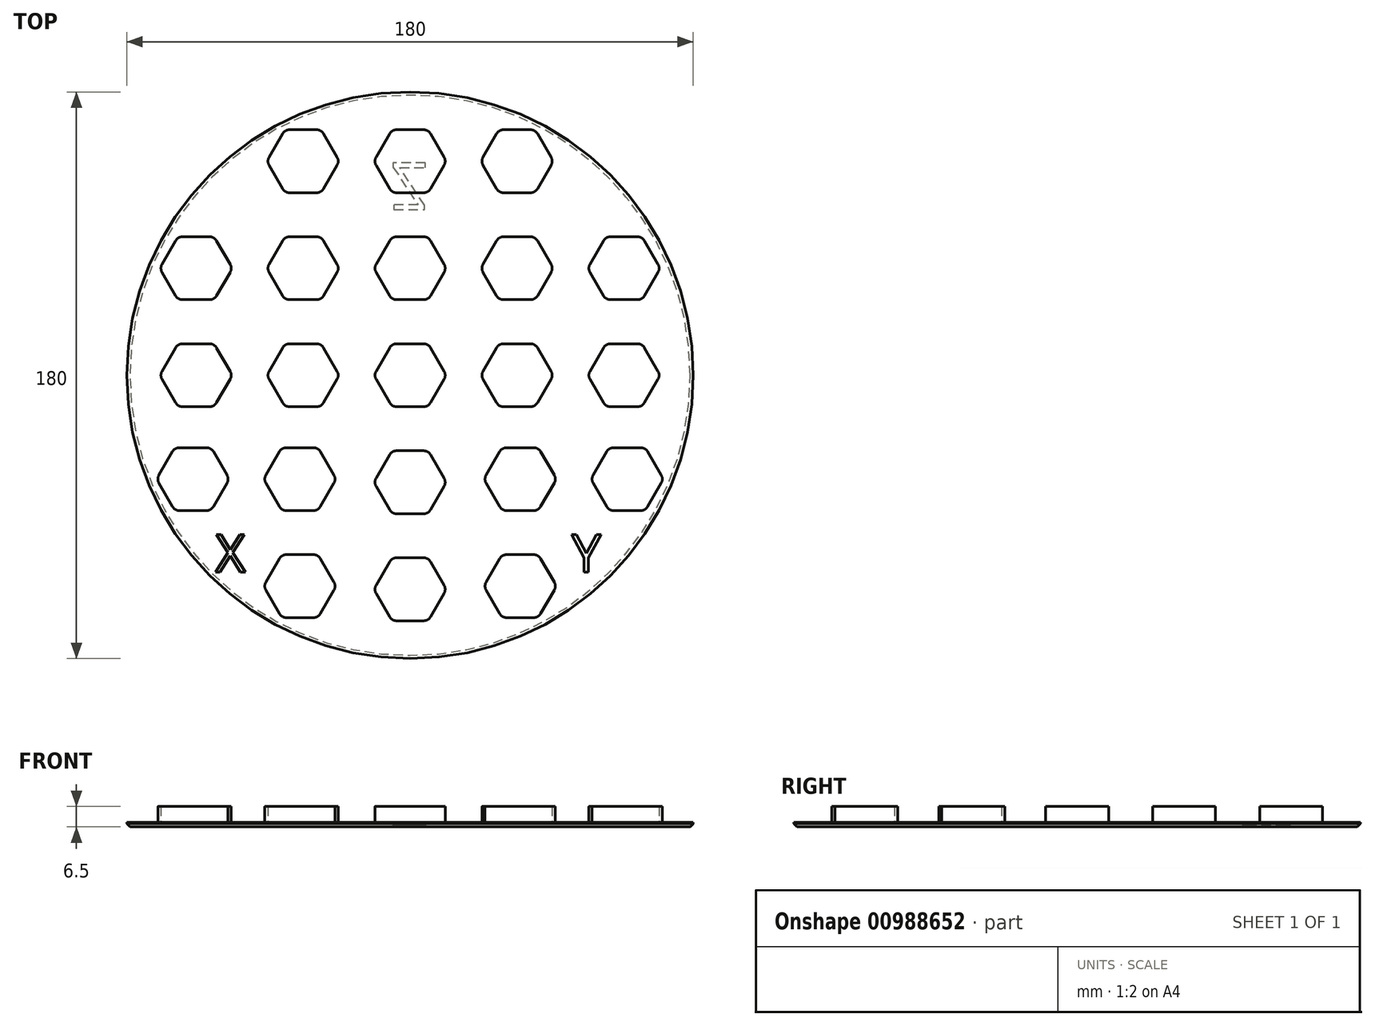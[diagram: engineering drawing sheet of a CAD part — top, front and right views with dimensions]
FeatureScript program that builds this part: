
annotation { "Feature Type Name" : "Feature", "Feature Type Description" : "" }
export const myFeature = defineFeature(function(context is Context, id is Id, definition is map)
    precondition{}
    {
        {
            var Q0;
            Q0=qCreatedBy(makeId("Top.planeOp"),FACE);
            var sketch = newSketch(context, id + "F0", { "sketchPlane" : qUnion([Q0])});
            skCircle(sketch, "E0", {"center": v(0, 0) * mm, "radius": 90 * mm});
            skSolve(sketch);
        }
        {
            var Q0;
            Q0 = qSketchRegion(id + "F0", true);
            extrude(context, id + "F1", {"entities" : qUnion([Q0]), "depth" : 1.5 * mm, "offsetDistance" : 25 * mm});
        }
        {
            var Q0;
            Q0=makeQuery(id+"F1.opExtrude","CAP_FACE",FACE,{"disambiguationData":[OSD([sQuery(id+"F0.wireOp",EDGE,"E0")])],"isStart":false});
            var sketch = newSketch(context, id + "F2", { "sketchPlane" : qUnion([Q0])});
            skCircle(sketch, "E1.cCircle", {"center": v(0, 0) * mm, "radius": 10 * mm, "construction": true});
            skLineSegment(sketch, "E1.0", {"start": v(-5.77, 10) * mm, "end": v(5.77, 10) * mm});
            skLineSegment(sketch, "E1.1", {"start": v(5.77, 10) * mm, "end": v(11.55, 0) * mm});
            skLineSegment(sketch, "E1.2", {"start": v(11.55, 0) * mm, "end": v(5.77, -10) * mm});
            skLineSegment(sketch, "E1.3", {"start": v(5.77, -10) * mm, "end": v(-5.77, -10) * mm});
            skLineSegment(sketch, "E1.4", {"start": v(-5.77, -10) * mm, "end": v(-11.55, 0) * mm});
            skLineSegment(sketch, "E1.5", {"start": v(-11.55, 0) * mm, "end": v(-5.77, 10) * mm});
            skPoint(sketch, "E1.0.midPoint", {"position": v(0, 10) * mm});
            skLineSegment(sketch, "E2", {"start": v(0, 0) * mm, "end": v(90, 0) * mm, "construction": true});
            skLineSegment(sketch, "E3", {"start": v(0, 0) * mm, "end": v(0, 90) * mm, "construction": true});
            skLineSegment(sketch, "E4.0.1.0", {"start": v(11.55, 34) * mm, "end": v(5.77, 24) * mm});
            skLineSegment(sketch, "E4.0.1.1", {"start": v(5.77, 24) * mm, "end": v(-5.77, 24) * mm});
            skPoint(sketch, "E4.0.1.2", {"position": v(0, 44) * mm});
            skCircle(sketch, "E4.0.1.3", {"center": v(0, 34) * mm, "radius": 10 * mm, "construction": true});
            skLineSegment(sketch, "E4.0.1.4", {"start": v(5.77, 44) * mm, "end": v(11.55, 34) * mm});
            skLineSegment(sketch, "E4.0.1.5", {"start": v(-5.77, 44) * mm, "end": v(5.77, 44) * mm});
            skLineSegment(sketch, "E4.0.1.6", {"start": v(-5.77, 24) * mm, "end": v(-11.55, 34) * mm});
            skLineSegment(sketch, "E4.0.1.7", {"start": v(-11.55, 34) * mm, "end": v(-5.77, 44) * mm});
            skLineSegment(sketch, "E4.0.2.0", {"start": v(11.55, 68) * mm, "end": v(5.77, 58) * mm});
            skLineSegment(sketch, "E4.0.2.1", {"start": v(5.77, 58) * mm, "end": v(-5.77, 58) * mm});
            skPoint(sketch, "E4.0.2.2", {"position": v(0, 78) * mm});
            skCircle(sketch, "E4.0.2.3", {"center": v(0, 68) * mm, "radius": 10 * mm, "construction": true});
            skLineSegment(sketch, "E4.0.2.4", {"start": v(5.77, 78) * mm, "end": v(11.55, 68) * mm});
            skLineSegment(sketch, "E4.0.2.5", {"start": v(-5.77, 78) * mm, "end": v(5.77, 78) * mm});
            skLineSegment(sketch, "E4.0.2.6", {"start": v(-5.77, 58) * mm, "end": v(-11.55, 68) * mm});
            skLineSegment(sketch, "E4.0.2.7", {"start": v(-11.55, 68) * mm, "end": v(-5.77, 78) * mm});
            skLineSegment(sketch, "E4.1.0.0", {"start": v(45.55, 0) * mm, "end": v(39.77, -10) * mm});
            skLineSegment(sketch, "E4.1.0.1", {"start": v(39.77, -10) * mm, "end": v(28.23, -10) * mm});
            skPoint(sketch, "E4.1.0.2", {"position": v(34, 10) * mm});
            skCircle(sketch, "E4.1.0.3", {"center": v(34, 0) * mm, "radius": 10 * mm, "construction": true});
            skLineSegment(sketch, "E4.1.0.4", {"start": v(39.77, 10) * mm, "end": v(45.55, 0) * mm});
            skLineSegment(sketch, "E4.1.0.5", {"start": v(28.23, 10) * mm, "end": v(39.77, 10) * mm});
            skLineSegment(sketch, "E4.1.0.6", {"start": v(28.23, -10) * mm, "end": v(22.45, 0) * mm});
            skLineSegment(sketch, "E4.1.0.7", {"start": v(22.45, 0) * mm, "end": v(28.23, 10) * mm});
            skLineSegment(sketch, "E4.1.1.0", {"start": v(45.55, 34) * mm, "end": v(39.77, 24) * mm});
            skLineSegment(sketch, "E4.1.1.1", {"start": v(39.77, 24) * mm, "end": v(28.23, 24) * mm});
            skPoint(sketch, "E4.1.1.2", {"position": v(34, 44) * mm});
            skCircle(sketch, "E4.1.1.3", {"center": v(34, 34) * mm, "radius": 10 * mm, "construction": true});
            skLineSegment(sketch, "E4.1.1.4", {"start": v(39.77, 44) * mm, "end": v(45.55, 34) * mm});
            skLineSegment(sketch, "E4.1.1.5", {"start": v(28.23, 44) * mm, "end": v(39.77, 44) * mm});
            skLineSegment(sketch, "E4.1.1.6", {"start": v(28.23, 24) * mm, "end": v(22.45, 34) * mm});
            skLineSegment(sketch, "E4.1.1.7", {"start": v(22.45, 34) * mm, "end": v(28.23, 44) * mm});
            skLineSegment(sketch, "E4.1.2.0", {"start": v(45.55, 68) * mm, "end": v(39.77, 58) * mm});
            skLineSegment(sketch, "E4.1.2.1", {"start": v(39.77, 58) * mm, "end": v(28.23, 58) * mm});
            skPoint(sketch, "E4.1.2.2", {"position": v(34, 78) * mm});
            skCircle(sketch, "E4.1.2.3", {"center": v(34, 68) * mm, "radius": 10 * mm, "construction": true});
            skLineSegment(sketch, "E4.1.2.4", {"start": v(39.77, 78) * mm, "end": v(45.55, 68) * mm});
            skLineSegment(sketch, "E4.1.2.5", {"start": v(28.23, 78) * mm, "end": v(39.77, 78) * mm});
            skLineSegment(sketch, "E4.1.2.6", {"start": v(28.23, 58) * mm, "end": v(22.45, 68) * mm});
            skLineSegment(sketch, "E4.1.2.7", {"start": v(22.45, 68) * mm, "end": v(28.23, 78) * mm});
            skLineSegment(sketch, "E4.2.0.0", {"start": v(79.55, 0) * mm, "end": v(73.77, -10) * mm});
            skLineSegment(sketch, "E4.2.0.1", {"start": v(73.77, -10) * mm, "end": v(62.23, -10) * mm});
            skPoint(sketch, "E4.2.0.2", {"position": v(68, 10) * mm});
            skCircle(sketch, "E4.2.0.3", {"center": v(68, 0) * mm, "radius": 10 * mm, "construction": true});
            skLineSegment(sketch, "E4.2.0.4", {"start": v(73.77, 10) * mm, "end": v(79.55, 0) * mm});
            skLineSegment(sketch, "E4.2.0.5", {"start": v(62.23, 10) * mm, "end": v(73.77, 10) * mm});
            skLineSegment(sketch, "E4.2.0.6", {"start": v(62.23, -10) * mm, "end": v(56.45, 0) * mm});
            skLineSegment(sketch, "E4.2.0.7", {"start": v(56.45, 0) * mm, "end": v(62.23, 10) * mm});
            skLineSegment(sketch, "E4.2.1.0", {"start": v(79.55, 34) * mm, "end": v(73.77, 24) * mm});
            skLineSegment(sketch, "E4.2.1.1", {"start": v(73.77, 24) * mm, "end": v(62.23, 24) * mm});
            skPoint(sketch, "E4.2.1.2", {"position": v(68, 44) * mm});
            skCircle(sketch, "E4.2.1.3", {"center": v(68, 34) * mm, "radius": 10 * mm, "construction": true});
            skLineSegment(sketch, "E4.2.1.4", {"start": v(73.77, 44) * mm, "end": v(79.55, 34) * mm});
            skLineSegment(sketch, "E4.2.1.5", {"start": v(62.23, 44) * mm, "end": v(73.77, 44) * mm});
            skLineSegment(sketch, "E4.2.1.6", {"start": v(62.23, 24) * mm, "end": v(56.45, 34) * mm});
            skLineSegment(sketch, "E4.2.1.7", {"start": v(56.45, 34) * mm, "end": v(62.23, 44) * mm});
            skLineSegment(sketch, "E4.direction1", {"start": v(-5.77, -10) * mm, "end": v(28.23, -10) * mm, "construction": true});
            skLineSegment(sketch, "E4.direction2", {"start": v(-5.77, -10) * mm, "end": v(-5.77, 24) * mm, "construction": true});
            skCircle(sketch, "E5.1.0", {"center": v(0, -34) * mm, "radius": 10 * mm, "construction": true});
            skLineSegment(sketch, "E5.1.1", {"start": v(11.55, -34) * mm, "end": v(5.77, -44) * mm});
            skLineSegment(sketch, "E5.1.2", {"start": v(-5.77, -58) * mm, "end": v(5.77, -58) * mm});
            skLineSegment(sketch, "E5.1.3", {"start": v(11.55, -68) * mm, "end": v(5.77, -78) * mm});
            skCircle(sketch, "E5.1.4", {"center": v(0, -68) * mm, "radius": 10 * mm, "construction": true});
            skLineSegment(sketch, "E5.1.5", {"start": v(-11.55, -68) * mm, "end": v(-5.77, -58) * mm});
            skPoint(sketch, "E5.1.6", {"position": v(0, -44) * mm});
            skLineSegment(sketch, "E5.1.7", {"start": v(5.77, -24) * mm, "end": v(11.55, -34) * mm});
            skPoint(sketch, "E5.1.8", {"position": v(0, -78) * mm});
            skLineSegment(sketch, "E5.1.9", {"start": v(-11.55, -34) * mm, "end": v(-5.77, -24) * mm});
            skLineSegment(sketch, "E5.1.10", {"start": v(5.77, -44) * mm, "end": v(-5.77, -44) * mm});
            skLineSegment(sketch, "E5.1.11", {"start": v(5.77, -58) * mm, "end": v(11.55, -68) * mm});
            skLineSegment(sketch, "E5.1.12", {"start": v(5.77, -78) * mm, "end": v(-5.77, -78) * mm});
            skLineSegment(sketch, "E5.1.13", {"start": v(-5.77, -24) * mm, "end": v(5.77, -24) * mm});
            skLineSegment(sketch, "E5.1.14", {"start": v(-5.77, -78) * mm, "end": v(-11.55, -68) * mm});
            skLineSegment(sketch, "E5.1.15", {"start": v(-5.77, -44) * mm, "end": v(-11.55, -34) * mm});
            skLineSegment(sketch, "E5.1.16", {"start": v(-39.77, 10) * mm, "end": v(-28.23, 10) * mm});
            skLineSegment(sketch, "E5.1.17", {"start": v(-56.45, 0) * mm, "end": v(-62.23, -10) * mm});
            skLineSegment(sketch, "E5.1.18", {"start": v(-28.23, -10) * mm, "end": v(-39.77, -10) * mm});
            skLineSegment(sketch, "E5.1.19", {"start": v(-22.45, 0) * mm, "end": v(-28.23, -10) * mm});
            skLineSegment(sketch, "E5.1.20", {"start": v(-45.55, 0) * mm, "end": v(-39.77, 10) * mm});
            skLineSegment(sketch, "E5.1.21", {"start": v(-73.77, 10) * mm, "end": v(-62.23, 10) * mm});
            skLineSegment(sketch, "E5.1.22", {"start": v(-62.23, 10) * mm, "end": v(-56.45, 0) * mm});
            skPoint(sketch, "E5.1.23", {"position": v(-68, -10) * mm});
            skCircle(sketch, "E5.1.24", {"center": v(-34, 0) * mm, "radius": 10 * mm, "construction": true});
            skCircle(sketch, "E5.1.25", {"center": v(-68, 0) * mm, "radius": 10 * mm, "construction": true});
            skLineSegment(sketch, "E5.1.26", {"start": v(-79.55, 0) * mm, "end": v(-73.77, 10) * mm});
            skLineSegment(sketch, "E5.1.27", {"start": v(-28.23, 10) * mm, "end": v(-22.45, 0) * mm});
            skPoint(sketch, "E5.1.28", {"position": v(-34, -10) * mm});
            skLineSegment(sketch, "E5.1.29", {"start": v(-62.23, -10) * mm, "end": v(-73.77, -10) * mm});
            skLineSegment(sketch, "E5.1.30", {"start": v(-39.77, -10) * mm, "end": v(-45.55, 0) * mm});
            skLineSegment(sketch, "E5.1.31", {"start": v(-73.77, -10) * mm, "end": v(-79.55, 0) * mm});
            skLineSegment(sketch, "E6.2.0", {"start": v(-29.23, -43) * mm, "end": v(-40.77, -43) * mm});
            skPoint(sketch, "E6.2.1", {"position": v(-35, -77) * mm});
            skLineSegment(sketch, "E6.2.2", {"start": v(-63.23, -23) * mm, "end": v(-57.45, -33) * mm});
            skLineSegment(sketch, "E6.2.3", {"start": v(-29.23, -57) * mm, "end": v(-23.45, -67) * mm});
            skPoint(sketch, "E6.2.4", {"position": v(-69, -43) * mm});
            skLineSegment(sketch, "E6.2.5", {"start": v(-40.77, -77) * mm, "end": v(-46.55, -67) * mm});
            skCircle(sketch, "E6.2.6", {"center": v(-35, -33) * mm, "radius": 10 * mm, "construction": true});
            skLineSegment(sketch, "E6.2.7", {"start": v(-74.77, -43) * mm, "end": v(-80.55, -33) * mm});
            skLineSegment(sketch, "E6.2.8", {"start": v(-40.77, -43) * mm, "end": v(-46.55, -33) * mm});
            skLineSegment(sketch, "E6.2.9", {"start": v(-80.55, -33) * mm, "end": v(-74.77, -23) * mm});
            skLineSegment(sketch, "E6.2.10", {"start": v(-40.77, -23) * mm, "end": v(-29.23, -23) * mm});
            skPoint(sketch, "E6.2.11", {"position": v(-35, -43) * mm});
            skLineSegment(sketch, "E6.2.12", {"start": v(-46.55, -67) * mm, "end": v(-40.77, -57) * mm});
            skLineSegment(sketch, "E6.2.13", {"start": v(-46.55, -33) * mm, "end": v(-40.77, -23) * mm});
            skLineSegment(sketch, "E6.2.14", {"start": v(-29.23, -23) * mm, "end": v(-23.45, -33) * mm});
            skLineSegment(sketch, "E6.2.15", {"start": v(-23.45, -67) * mm, "end": v(-29.23, -77) * mm});
            skLineSegment(sketch, "E6.2.16", {"start": v(-63.23, -43) * mm, "end": v(-74.77, -43) * mm});
            skLineSegment(sketch, "E6.2.17", {"start": v(-23.45, -33) * mm, "end": v(-29.23, -43) * mm});
            skLineSegment(sketch, "E6.2.18", {"start": v(-29.23, -77) * mm, "end": v(-40.77, -77) * mm});
            skCircle(sketch, "E6.2.19", {"center": v(-69, -33) * mm, "radius": 10 * mm, "construction": true});
            skLineSegment(sketch, "E6.2.20", {"start": v(-57.45, -33) * mm, "end": v(-63.23, -43) * mm});
            skLineSegment(sketch, "E6.2.21", {"start": v(-40.77, -57) * mm, "end": v(-29.23, -57) * mm});
            skCircle(sketch, "E6.2.22", {"center": v(-35, -67) * mm, "radius": 10 * mm, "construction": true});
            skLineSegment(sketch, "E6.2.23", {"start": v(-74.77, -23) * mm, "end": v(-63.23, -23) * mm});
            skPoint(sketch, "E6.center", {"position": v(-0.5, 0.5) * mm});
            skLineSegment(sketch, "E7.MirrorCS", {"start": v(-28.23, 24) * mm, "end": v(-22.45, 34) * mm});
            skLineSegment(sketch, "E8.MirrorCS", {"start": v(-28.23, 78) * mm, "end": v(-39.77, 78) * mm});
            skLineSegment(sketch, "E9.MirrorCS", {"start": v(-28.23, 44) * mm, "end": v(-39.77, 44) * mm});
            skLineSegment(sketch, "E10.MirrorCS", {"start": v(-62.23, 44) * mm, "end": v(-73.77, 44) * mm});
            skLineSegment(sketch, "E11.MirrorCS", {"start": v(-39.77, 44) * mm, "end": v(-45.55, 34) * mm});
            skLineSegment(sketch, "E12.MirrorCS", {"start": v(-73.77, 24) * mm, "end": v(-62.23, 24) * mm});
            skLineSegment(sketch, "E13.MirrorCS", {"start": v(-62.23, 24) * mm, "end": v(-56.45, 34) * mm});
            skLineSegment(sketch, "E14.MirrorCS", {"start": v(-39.77, 24) * mm, "end": v(-28.23, 24) * mm});
            skLineSegment(sketch, "E15.MirrorCS", {"start": v(-73.77, 44) * mm, "end": v(-79.55, 34) * mm});
            skLineSegment(sketch, "E16.MirrorCS", {"start": v(-45.55, 68) * mm, "end": v(-39.77, 58) * mm});
            skPoint(sketch, "E17.MirrorP", {"position": v(-34, 44) * mm});
            skLineSegment(sketch, "E18.MirrorCS", {"start": v(-22.45, 68) * mm, "end": v(-28.23, 78) * mm});
            skCircle(sketch, "E19.MirrorC", {"center": v(-34, 68) * mm, "radius": 10 * mm, "construction": true});
            skLineSegment(sketch, "E20.MirrorCS", {"start": v(-79.55, 34) * mm, "end": v(-73.77, 24) * mm});
            skPoint(sketch, "E21.MirrorP", {"position": v(-34, 78) * mm});
            skLineSegment(sketch, "E22.MirrorCS", {"start": v(-28.23, 58) * mm, "end": v(-22.45, 68) * mm});
            skPoint(sketch, "E23.MirrorP", {"position": v(-68, 44) * mm});
            skLineSegment(sketch, "E24.MirrorCS", {"start": v(-39.77, 58) * mm, "end": v(-28.23, 58) * mm});
            skCircle(sketch, "E25.MirrorC", {"center": v(-68, 34) * mm, "radius": 10 * mm, "construction": true});
            skLineSegment(sketch, "E26.MirrorCS", {"start": v(-45.55, 34) * mm, "end": v(-39.77, 24) * mm});
            skLineSegment(sketch, "E27.MirrorCS", {"start": v(-22.45, 34) * mm, "end": v(-28.23, 44) * mm});
            skLineSegment(sketch, "E28.MirrorCS", {"start": v(-39.77, 78) * mm, "end": v(-45.55, 68) * mm});
            skCircle(sketch, "E29.MirrorC", {"center": v(-34, 34) * mm, "radius": 10 * mm, "construction": true});
            skLineSegment(sketch, "E30.MirrorCS", {"start": v(-56.45, 34) * mm, "end": v(-62.23, 44) * mm});
            skLineSegment(sketch, "E31.MirrorCS", {"start": v(63.23, -43) * mm, "end": v(74.77, -43) * mm});
            skLineSegment(sketch, "E32.MirrorCS", {"start": v(74.77, -43) * mm, "end": v(80.55, -33) * mm});
            skLineSegment(sketch, "E33.MirrorCS", {"start": v(80.55, -33) * mm, "end": v(74.77, -23) * mm});
            skLineSegment(sketch, "E34.MirrorCS", {"start": v(29.23, -77) * mm, "end": v(40.77, -77) * mm});
            skLineSegment(sketch, "E35.MirrorCS", {"start": v(74.77, -23) * mm, "end": v(63.23, -23) * mm});
            skLineSegment(sketch, "E36.MirrorCS", {"start": v(29.23, -43) * mm, "end": v(40.77, -43) * mm});
            skLineSegment(sketch, "E37.MirrorCS", {"start": v(57.45, -33) * mm, "end": v(63.23, -43) * mm});
            skPoint(sketch, "E38.MirrorP", {"position": v(69, -43) * mm});
            skLineSegment(sketch, "E39.MirrorCS", {"start": v(29.23, -57) * mm, "end": v(23.45, -67) * mm});
            skLineSegment(sketch, "E40.MirrorCS", {"start": v(40.77, -23) * mm, "end": v(29.23, -23) * mm});
            skLineSegment(sketch, "E41.MirrorCS", {"start": v(40.77, -57) * mm, "end": v(29.23, -57) * mm});
            skCircle(sketch, "E42.MirrorC", {"center": v(35, -33) * mm, "radius": 10 * mm, "construction": true});
            skLineSegment(sketch, "E43.MirrorCS", {"start": v(23.45, -67) * mm, "end": v(29.23, -77) * mm});
            skLineSegment(sketch, "E44.MirrorCS", {"start": v(63.23, -23) * mm, "end": v(57.45, -33) * mm});
            skLineSegment(sketch, "E45.MirrorCS", {"start": v(46.55, -67) * mm, "end": v(40.77, -57) * mm});
            skCircle(sketch, "E46.MirrorC", {"center": v(69, -33) * mm, "radius": 10 * mm, "construction": true});
            skPoint(sketch, "E47.MirrorP", {"position": v(35, -43) * mm});
            skLineSegment(sketch, "E48.MirrorCS", {"start": v(29.23, -23) * mm, "end": v(23.45, -33) * mm});
            skPoint(sketch, "E49.MirrorP", {"position": v(35, -77) * mm});
            skLineSegment(sketch, "E50.MirrorCS", {"start": v(40.77, -43) * mm, "end": v(46.55, -33) * mm});
            skLineSegment(sketch, "E51.MirrorCS", {"start": v(40.77, -77) * mm, "end": v(46.55, -67) * mm});
            skLineSegment(sketch, "E52.MirrorCS", {"start": v(46.55, -33) * mm, "end": v(40.77, -23) * mm});
            skLineSegment(sketch, "E53.MirrorCS", {"start": v(23.45, -33) * mm, "end": v(29.23, -43) * mm});
            skCircle(sketch, "E54.MirrorC", {"center": v(35, -67) * mm, "radius": 10 * mm, "construction": true});
            skSolve(sketch);
        }
        {
            var Q0;
            Q0 = qSketchRegion(id + "F2", true);
            extrude(context, id + "F3", {"entities" : qUnion([Q0]), "operationType" : NewBodyOperationType.ADD, "depth" : 5 * mm, "offsetDistance" : 25 * mm});
        }
        {
            var Q0;
            Q0=makeQuery(id+"F3.opExtrude","SWEPT_EDGE",EDGE,{"disambiguationData":[OSD([sQuery(id+"F2.wireOp",EDGE,"E6.2.5"),sQuery(id+"F2.wireOp",EDGE,"E6.2.18")])]});
            var Q1;
            Q1=makeQuery(id+"F3.opExtrude","SWEPT_EDGE",EDGE,{"disambiguationData":[OSD([sQuery(id+"F2.wireOp",EDGE,"E6.2.15"),sQuery(id+"F2.wireOp",EDGE,"E6.2.18")])]});
            var Q2;
            Q2=makeQuery(id+"F3.opExtrude","SWEPT_EDGE",EDGE,{"disambiguationData":[OSD([sQuery(id+"F2.wireOp",EDGE,"E6.2.3"),sQuery(id+"F2.wireOp",EDGE,"E6.2.15")])]});
            var Q3;
            Q3=makeQuery(id+"F3.opExtrude","SWEPT_EDGE",EDGE,{"disambiguationData":[OSD([sQuery(id+"F2.wireOp",EDGE,"E6.2.5"),sQuery(id+"F2.wireOp",EDGE,"E6.2.12")])]});
            var Q4;
            Q4=makeQuery(id+"F3.opExtrude","SWEPT_EDGE",EDGE,{"disambiguationData":[OSD([sQuery(id+"F2.wireOp",EDGE,"E6.2.12"),sQuery(id+"F2.wireOp",EDGE,"E6.2.21")])]});
            var Q5;
            Q5=makeQuery(id+"F3.opExtrude","SWEPT_EDGE",EDGE,{"disambiguationData":[OSD([sQuery(id+"F2.wireOp",EDGE,"E6.2.3"),sQuery(id+"F2.wireOp",EDGE,"E6.2.21")])]});
            var Q6;
            Q6=makeQuery(id+"F3.opExtrude","SWEPT_EDGE",EDGE,{"disambiguationData":[OSD([sQuery(id+"F2.wireOp",EDGE,"E5.1.12"),sQuery(id+"F2.wireOp",EDGE,"E5.1.14")])]});
            var Q7;
            Q7=makeQuery(id+"F3.opExtrude","SWEPT_EDGE",EDGE,{"disambiguationData":[OSD([sQuery(id+"F2.wireOp",EDGE,"E5.1.3"),sQuery(id+"F2.wireOp",EDGE,"E5.1.12")])]});
            var Q8;
            Q8=makeQuery(id+"F3.opExtrude","SWEPT_EDGE",EDGE,{"disambiguationData":[OSD([sQuery(id+"F2.wireOp",EDGE,"E5.1.3"),sQuery(id+"F2.wireOp",EDGE,"E5.1.11")])]});
            var Q9;
            Q9=makeQuery(id+"F3.opExtrude","SWEPT_EDGE",EDGE,{"disambiguationData":[OSD([sQuery(id+"F2.wireOp",EDGE,"E5.1.5"),sQuery(id+"F2.wireOp",EDGE,"E5.1.14")])]});
            var Q10;
            Q10=makeQuery(id+"F3.opExtrude","SWEPT_EDGE",EDGE,{"disambiguationData":[OSD([sQuery(id+"F2.wireOp",EDGE,"E5.1.2"),sQuery(id+"F2.wireOp",EDGE,"E5.1.5")])]});
            var Q11;
            Q11=makeQuery(id+"F3.opExtrude","SWEPT_EDGE",EDGE,{"disambiguationData":[OSD([sQuery(id+"F2.wireOp",EDGE,"E5.1.2"),sQuery(id+"F2.wireOp",EDGE,"E5.1.11")])]});
            var Q12;
            Q12=makeQuery(id+"F3.opExtrude","SWEPT_EDGE",EDGE,{"disambiguationData":[OSD([sQuery(id+"F2.wireOp",EDGE,"E39.MirrorCS"),sQuery(id+"F2.wireOp",EDGE,"E43.MirrorCS")])]});
            var Q13;
            Q13=makeQuery(id+"F3.opExtrude","SWEPT_EDGE",EDGE,{"disambiguationData":[OSD([sQuery(id+"F2.wireOp",EDGE,"E39.MirrorCS"),sQuery(id+"F2.wireOp",EDGE,"E41.MirrorCS")])]});
            var Q14;
            Q14=makeQuery(id+"F3.opExtrude","SWEPT_EDGE",EDGE,{"disambiguationData":[OSD([sQuery(id+"F2.wireOp",EDGE,"E41.MirrorCS"),sQuery(id+"F2.wireOp",EDGE,"E45.MirrorCS")])]});
            var Q15;
            Q15=makeQuery(id+"F3.opExtrude","SWEPT_EDGE",EDGE,{"disambiguationData":[OSD([sQuery(id+"F2.wireOp",EDGE,"E34.MirrorCS"),sQuery(id+"F2.wireOp",EDGE,"E43.MirrorCS")])]});
            var Q16;
            Q16=makeQuery(id+"F3.opExtrude","SWEPT_EDGE",EDGE,{"disambiguationData":[OSD([sQuery(id+"F2.wireOp",EDGE,"E45.MirrorCS"),sQuery(id+"F2.wireOp",EDGE,"E51.MirrorCS")])]});
            var Q17;
            Q17=makeQuery(id+"F3.opExtrude","SWEPT_EDGE",EDGE,{"disambiguationData":[OSD([sQuery(id+"F2.wireOp",EDGE,"E34.MirrorCS"),sQuery(id+"F2.wireOp",EDGE,"E51.MirrorCS")])]});
            var Q18;
            Q18=makeQuery(id+"F3.opExtrude","SWEPT_EDGE",EDGE,{"disambiguationData":[OSD([sQuery(id+"F2.wireOp",EDGE,"E6.2.7"),sQuery(id+"F2.wireOp",EDGE,"E6.2.16")])]});
            var Q19;
            Q19=makeQuery(id+"F3.opExtrude","SWEPT_EDGE",EDGE,{"disambiguationData":[OSD([sQuery(id+"F2.wireOp",EDGE,"E6.2.16"),sQuery(id+"F2.wireOp",EDGE,"E6.2.20")])]});
            var Q20;
            Q20=makeQuery(id+"F3.opExtrude","SWEPT_EDGE",EDGE,{"disambiguationData":[OSD([sQuery(id+"F2.wireOp",EDGE,"E6.2.2"),sQuery(id+"F2.wireOp",EDGE,"E6.2.20")])]});
            var Q21;
            Q21=makeQuery(id+"F3.opExtrude","SWEPT_EDGE",EDGE,{"disambiguationData":[OSD([sQuery(id+"F2.wireOp",EDGE,"E6.2.2"),sQuery(id+"F2.wireOp",EDGE,"E6.2.23")])]});
            var Q22;
            Q22=makeQuery(id+"F3.opExtrude","SWEPT_EDGE",EDGE,{"disambiguationData":[OSD([sQuery(id+"F2.wireOp",EDGE,"E6.2.9"),sQuery(id+"F2.wireOp",EDGE,"E6.2.23")])]});
            var Q23;
            Q23=makeQuery(id+"F3.opExtrude","SWEPT_EDGE",EDGE,{"disambiguationData":[OSD([sQuery(id+"F2.wireOp",EDGE,"E6.2.7"),sQuery(id+"F2.wireOp",EDGE,"E6.2.9")])]});
            var Q24;
            Q24=makeQuery(id+"F3.opExtrude","SWEPT_EDGE",EDGE,{"disambiguationData":[OSD([sQuery(id+"F2.wireOp",EDGE,"E6.2.10"),sQuery(id+"F2.wireOp",EDGE,"E6.2.13")])]});
            var Q25;
            Q25=makeQuery(id+"F3.opExtrude","SWEPT_EDGE",EDGE,{"disambiguationData":[OSD([sQuery(id+"F2.wireOp",EDGE,"E6.2.8"),sQuery(id+"F2.wireOp",EDGE,"E6.2.13")])]});
            var Q26;
            Q26=makeQuery(id+"F3.opExtrude","SWEPT_EDGE",EDGE,{"disambiguationData":[OSD([sQuery(id+"F2.wireOp",EDGE,"E6.2.0"),sQuery(id+"F2.wireOp",EDGE,"E6.2.8")])]});
            var Q27;
            Q27=makeQuery(id+"F3.opExtrude","SWEPT_EDGE",EDGE,{"disambiguationData":[OSD([sQuery(id+"F2.wireOp",EDGE,"E6.2.0"),sQuery(id+"F2.wireOp",EDGE,"E6.2.17")])]});
            var Q28;
            Q28=makeQuery(id+"F3.opExtrude","SWEPT_EDGE",EDGE,{"disambiguationData":[OSD([sQuery(id+"F2.wireOp",EDGE,"E6.2.14"),sQuery(id+"F2.wireOp",EDGE,"E6.2.17")])]});
            var Q29;
            Q29=makeQuery(id+"F3.opExtrude","SWEPT_EDGE",EDGE,{"disambiguationData":[OSD([sQuery(id+"F2.wireOp",EDGE,"E6.2.10"),sQuery(id+"F2.wireOp",EDGE,"E6.2.14")])]});
            var Q30;
            Q30=makeQuery(id+"F3.opExtrude","SWEPT_EDGE",EDGE,{"disambiguationData":[OSD([sQuery(id+"F2.wireOp",EDGE,"E5.1.9"),sQuery(id+"F2.wireOp",EDGE,"E5.1.15")])]});
            var Q31;
            Q31=makeQuery(id+"F3.opExtrude","SWEPT_EDGE",EDGE,{"disambiguationData":[OSD([sQuery(id+"F2.wireOp",EDGE,"E5.1.9"),sQuery(id+"F2.wireOp",EDGE,"E5.1.13")])]});
            var Q32;
            Q32=makeQuery(id+"F3.opExtrude","SWEPT_EDGE",EDGE,{"disambiguationData":[OSD([sQuery(id+"F2.wireOp",EDGE,"E5.1.10"),sQuery(id+"F2.wireOp",EDGE,"E5.1.15")])]});
            var Q33;
            Q33=makeQuery(id+"F3.opExtrude","SWEPT_EDGE",EDGE,{"disambiguationData":[OSD([sQuery(id+"F2.wireOp",EDGE,"E5.1.1"),sQuery(id+"F2.wireOp",EDGE,"E5.1.10")])]});
            var Q34;
            Q34=makeQuery(id+"F3.opExtrude","SWEPT_EDGE",EDGE,{"disambiguationData":[OSD([sQuery(id+"F2.wireOp",EDGE,"E5.1.1"),sQuery(id+"F2.wireOp",EDGE,"E5.1.7")])]});
            var Q35;
            Q35=makeQuery(id+"F3.opExtrude","SWEPT_EDGE",EDGE,{"disambiguationData":[OSD([sQuery(id+"F2.wireOp",EDGE,"E5.1.7"),sQuery(id+"F2.wireOp",EDGE,"E5.1.13")])]});
            var Q36;
            Q36=makeQuery(id+"F3.opExtrude","SWEPT_EDGE",EDGE,{"disambiguationData":[OSD([sQuery(id+"F2.wireOp",EDGE,"E48.MirrorCS"),sQuery(id+"F2.wireOp",EDGE,"E53.MirrorCS")])]});
            var Q37;
            Q37=makeQuery(id+"F3.opExtrude","SWEPT_EDGE",EDGE,{"disambiguationData":[OSD([sQuery(id+"F2.wireOp",EDGE,"E36.MirrorCS"),sQuery(id+"F2.wireOp",EDGE,"E53.MirrorCS")])]});
            var Q38;
            Q38=makeQuery(id+"F3.opExtrude","SWEPT_EDGE",EDGE,{"disambiguationData":[OSD([sQuery(id+"F2.wireOp",EDGE,"E50.MirrorCS"),sQuery(id+"F2.wireOp",EDGE,"E52.MirrorCS")])]});
            var Q39;
            Q39=makeQuery(id+"F3.opExtrude","SWEPT_EDGE",EDGE,{"disambiguationData":[OSD([sQuery(id+"F2.wireOp",EDGE,"E40.MirrorCS"),sQuery(id+"F2.wireOp",EDGE,"E52.MirrorCS")])]});
            var Q40;
            Q40=makeQuery(id+"F3.opExtrude","SWEPT_EDGE",EDGE,{"disambiguationData":[OSD([sQuery(id+"F2.wireOp",EDGE,"E40.MirrorCS"),sQuery(id+"F2.wireOp",EDGE,"E48.MirrorCS")])]});
            var Q41;
            Q41=makeQuery(id+"F3.opExtrude","SWEPT_EDGE",EDGE,{"disambiguationData":[OSD([sQuery(id+"F2.wireOp",EDGE,"E36.MirrorCS"),sQuery(id+"F2.wireOp",EDGE,"E50.MirrorCS")])]});
            var Q42;
            Q42=makeQuery(id+"F3.opExtrude","SWEPT_EDGE",EDGE,{"disambiguationData":[OSD([sQuery(id+"F2.wireOp",EDGE,"E31.MirrorCS"),sQuery(id+"F2.wireOp",EDGE,"E37.MirrorCS")])]});
            var Q43;
            Q43=makeQuery(id+"F3.opExtrude","SWEPT_EDGE",EDGE,{"disambiguationData":[OSD([sQuery(id+"F2.wireOp",EDGE,"E31.MirrorCS"),sQuery(id+"F2.wireOp",EDGE,"E32.MirrorCS")])]});
            var Q44;
            Q44=makeQuery(id+"F3.opExtrude","SWEPT_EDGE",EDGE,{"disambiguationData":[OSD([sQuery(id+"F2.wireOp",EDGE,"E32.MirrorCS"),sQuery(id+"F2.wireOp",EDGE,"E33.MirrorCS")])]});
            var Q45;
            Q45=makeQuery(id+"F3.opExtrude","SWEPT_EDGE",EDGE,{"disambiguationData":[OSD([sQuery(id+"F2.wireOp",EDGE,"E33.MirrorCS"),sQuery(id+"F2.wireOp",EDGE,"E35.MirrorCS")])]});
            var Q46;
            Q46=makeQuery(id+"F3.opExtrude","SWEPT_EDGE",EDGE,{"disambiguationData":[OSD([sQuery(id+"F2.wireOp",EDGE,"E35.MirrorCS"),sQuery(id+"F2.wireOp",EDGE,"E44.MirrorCS")])]});
            var Q47;
            Q47=makeQuery(id+"F3.opExtrude","SWEPT_EDGE",EDGE,{"disambiguationData":[OSD([sQuery(id+"F2.wireOp",EDGE,"E37.MirrorCS"),sQuery(id+"F2.wireOp",EDGE,"E44.MirrorCS")])]});
            var Q48;
            Q48=makeQuery(id+"F3.opExtrude","SWEPT_EDGE",EDGE,{"disambiguationData":[OSD([sQuery(id+"F2.wireOp",EDGE,"E4.2.0.0"),sQuery(id+"F2.wireOp",EDGE,"E4.2.0.1")])]});
            var Q49;
            Q49=makeQuery(id+"F3.opExtrude","SWEPT_EDGE",EDGE,{"disambiguationData":[OSD([sQuery(id+"F2.wireOp",EDGE,"E4.2.0.1"),sQuery(id+"F2.wireOp",EDGE,"E4.2.0.6")])]});
            var Q50;
            Q50=makeQuery(id+"F3.opExtrude","SWEPT_EDGE",EDGE,{"disambiguationData":[OSD([sQuery(id+"F2.wireOp",EDGE,"E4.2.0.0"),sQuery(id+"F2.wireOp",EDGE,"E4.2.0.4")])]});
            var Q51;
            Q51=makeQuery(id+"F3.opExtrude","SWEPT_EDGE",EDGE,{"disambiguationData":[OSD([sQuery(id+"F2.wireOp",EDGE,"E4.2.0.6"),sQuery(id+"F2.wireOp",EDGE,"E4.2.0.7")])]});
            var Q52;
            Q52=makeQuery(id+"F3.opExtrude","SWEPT_EDGE",EDGE,{"disambiguationData":[OSD([sQuery(id+"F2.wireOp",EDGE,"E4.2.0.5"),sQuery(id+"F2.wireOp",EDGE,"E4.2.0.7")])]});
            var Q53;
            Q53=makeQuery(id+"F3.opExtrude","SWEPT_EDGE",EDGE,{"disambiguationData":[OSD([sQuery(id+"F2.wireOp",EDGE,"E4.2.0.4"),sQuery(id+"F2.wireOp",EDGE,"E4.2.0.5")])]});
            var Q54;
            Q54=makeQuery(id+"F3.opExtrude","SWEPT_EDGE",EDGE,{"disambiguationData":[OSD([sQuery(id+"F2.wireOp",EDGE,"E4.1.0.4"),sQuery(id+"F2.wireOp",EDGE,"E4.1.0.5")])]});
            var Q55;
            Q55=makeQuery(id+"F3.opExtrude","SWEPT_EDGE",EDGE,{"disambiguationData":[OSD([sQuery(id+"F2.wireOp",EDGE,"E4.1.0.5"),sQuery(id+"F2.wireOp",EDGE,"E4.1.0.7")])]});
            var Q56;
            Q56=makeQuery(id+"F3.opExtrude","SWEPT_EDGE",EDGE,{"disambiguationData":[OSD([sQuery(id+"F2.wireOp",EDGE,"E4.1.0.6"),sQuery(id+"F2.wireOp",EDGE,"E4.1.0.7")])]});
            var Q57;
            Q57=makeQuery(id+"F3.opExtrude","SWEPT_EDGE",EDGE,{"disambiguationData":[OSD([sQuery(id+"F2.wireOp",EDGE,"E4.1.0.1"),sQuery(id+"F2.wireOp",EDGE,"E4.1.0.6")])]});
            var Q58;
            Q58=makeQuery(id+"F3.opExtrude","SWEPT_EDGE",EDGE,{"disambiguationData":[OSD([sQuery(id+"F2.wireOp",EDGE,"E4.1.0.0"),sQuery(id+"F2.wireOp",EDGE,"E4.1.0.1")])]});
            var Q59;
            Q59=makeQuery(id+"F3.opExtrude","SWEPT_EDGE",EDGE,{"disambiguationData":[OSD([sQuery(id+"F2.wireOp",EDGE,"E4.1.0.0"),sQuery(id+"F2.wireOp",EDGE,"E4.1.0.4")])]});
            var Q60;
            Q60=makeQuery(id+"F3.opExtrude","SWEPT_EDGE",EDGE,{"disambiguationData":[OSD([sQuery(id+"F2.wireOp",EDGE,"E1.2"),sQuery(id+"F2.wireOp",EDGE,"E1.3")])]});
            var Q61;
            Q61=makeQuery(id+"F3.opExtrude","SWEPT_EDGE",EDGE,{"disambiguationData":[OSD([sQuery(id+"F2.wireOp",EDGE,"E1.1"),sQuery(id+"F2.wireOp",EDGE,"E1.2")])]});
            var Q62;
            Q62=makeQuery(id+"F3.opExtrude","SWEPT_EDGE",EDGE,{"disambiguationData":[OSD([sQuery(id+"F2.wireOp",EDGE,"E1.3"),sQuery(id+"F2.wireOp",EDGE,"E1.4")])]});
            var Q63;
            Q63=makeQuery(id+"F3.opExtrude","SWEPT_EDGE",EDGE,{"disambiguationData":[OSD([sQuery(id+"F2.wireOp",EDGE,"E1.4"),sQuery(id+"F2.wireOp",EDGE,"E1.5")])]});
            var Q64;
            Q64=makeQuery(id+"F3.opExtrude","SWEPT_EDGE",EDGE,{"disambiguationData":[OSD([sQuery(id+"F2.wireOp",EDGE,"E1.0"),sQuery(id+"F2.wireOp",EDGE,"E1.5")])]});
            var Q65;
            Q65=makeQuery(id+"F3.opExtrude","SWEPT_EDGE",EDGE,{"disambiguationData":[OSD([sQuery(id+"F2.wireOp",EDGE,"E1.0"),sQuery(id+"F2.wireOp",EDGE,"E1.1")])]});
            var Q66;
            Q66=makeQuery(id+"F3.opExtrude","SWEPT_EDGE",EDGE,{"disambiguationData":[OSD([sQuery(id+"F2.wireOp",EDGE,"E5.1.16"),sQuery(id+"F2.wireOp",EDGE,"E5.1.20")])]});
            var Q67;
            Q67=makeQuery(id+"F3.opExtrude","SWEPT_EDGE",EDGE,{"disambiguationData":[OSD([sQuery(id+"F2.wireOp",EDGE,"E5.1.20"),sQuery(id+"F2.wireOp",EDGE,"E5.1.30")])]});
            var Q68;
            Q68=makeQuery(id+"F3.opExtrude","SWEPT_EDGE",EDGE,{"disambiguationData":[OSD([sQuery(id+"F2.wireOp",EDGE,"E5.1.18"),sQuery(id+"F2.wireOp",EDGE,"E5.1.30")])]});
            var Q69;
            Q69=makeQuery(id+"F3.opExtrude","SWEPT_EDGE",EDGE,{"disambiguationData":[OSD([sQuery(id+"F2.wireOp",EDGE,"E5.1.16"),sQuery(id+"F2.wireOp",EDGE,"E5.1.27")])]});
            var Q70;
            Q70=makeQuery(id+"F3.opExtrude","SWEPT_EDGE",EDGE,{"disambiguationData":[OSD([sQuery(id+"F2.wireOp",EDGE,"E5.1.19"),sQuery(id+"F2.wireOp",EDGE,"E5.1.27")])]});
            var Q71;
            Q71=makeQuery(id+"F3.opExtrude","SWEPT_EDGE",EDGE,{"disambiguationData":[OSD([sQuery(id+"F2.wireOp",EDGE,"E5.1.18"),sQuery(id+"F2.wireOp",EDGE,"E5.1.19")])]});
            var Q72;
            Q72=makeQuery(id+"F3.opExtrude","SWEPT_EDGE",EDGE,{"disambiguationData":[OSD([sQuery(id+"F2.wireOp",EDGE,"E5.1.29"),sQuery(id+"F2.wireOp",EDGE,"E5.1.31")])]});
            var Q73;
            Q73=makeQuery(id+"F3.opExtrude","SWEPT_EDGE",EDGE,{"disambiguationData":[OSD([sQuery(id+"F2.wireOp",EDGE,"E5.1.17"),sQuery(id+"F2.wireOp",EDGE,"E5.1.29")])]});
            var Q74;
            Q74=makeQuery(id+"F3.opExtrude","SWEPT_EDGE",EDGE,{"disambiguationData":[OSD([sQuery(id+"F2.wireOp",EDGE,"E5.1.17"),sQuery(id+"F2.wireOp",EDGE,"E5.1.22")])]});
            var Q75;
            Q75=makeQuery(id+"F3.opExtrude","SWEPT_EDGE",EDGE,{"disambiguationData":[OSD([sQuery(id+"F2.wireOp",EDGE,"E5.1.21"),sQuery(id+"F2.wireOp",EDGE,"E5.1.22")])]});
            var Q76;
            Q76=makeQuery(id+"F3.opExtrude","SWEPT_EDGE",EDGE,{"disambiguationData":[OSD([sQuery(id+"F2.wireOp",EDGE,"E5.1.21"),sQuery(id+"F2.wireOp",EDGE,"E5.1.26")])]});
            var Q77;
            Q77=makeQuery(id+"F3.opExtrude","SWEPT_EDGE",EDGE,{"disambiguationData":[OSD([sQuery(id+"F2.wireOp",EDGE,"E5.1.26"),sQuery(id+"F2.wireOp",EDGE,"E5.1.31")])]});
            var Q78;
            Q78=makeQuery(id+"F3.opExtrude","SWEPT_EDGE",EDGE,{"disambiguationData":[OSD([sQuery(id+"F2.wireOp",EDGE,"E10.MirrorCS"),sQuery(id+"F2.wireOp",EDGE,"E30.MirrorCS")])]});
            var Q79;
            Q79=makeQuery(id+"F3.opExtrude","SWEPT_EDGE",EDGE,{"disambiguationData":[OSD([sQuery(id+"F2.wireOp",EDGE,"E10.MirrorCS"),sQuery(id+"F2.wireOp",EDGE,"E15.MirrorCS")])]});
            var Q80;
            Q80=makeQuery(id+"F3.opExtrude","SWEPT_EDGE",EDGE,{"disambiguationData":[OSD([sQuery(id+"F2.wireOp",EDGE,"E15.MirrorCS"),sQuery(id+"F2.wireOp",EDGE,"E20.MirrorCS")])]});
            var Q81;
            Q81=makeQuery(id+"F3.opExtrude","SWEPT_EDGE",EDGE,{"disambiguationData":[OSD([sQuery(id+"F2.wireOp",EDGE,"E12.MirrorCS"),sQuery(id+"F2.wireOp",EDGE,"E20.MirrorCS")])]});
            var Q82;
            Q82=makeQuery(id+"F3.opExtrude","SWEPT_EDGE",EDGE,{"disambiguationData":[OSD([sQuery(id+"F2.wireOp",EDGE,"E13.MirrorCS"),sQuery(id+"F2.wireOp",EDGE,"E30.MirrorCS")])]});
            var Q83;
            Q83=makeQuery(id+"F3.opExtrude","SWEPT_EDGE",EDGE,{"disambiguationData":[OSD([sQuery(id+"F2.wireOp",EDGE,"E12.MirrorCS"),sQuery(id+"F2.wireOp",EDGE,"E13.MirrorCS")])]});
            var Q84;
            Q84=makeQuery(id+"F3.opExtrude","SWEPT_EDGE",EDGE,{"disambiguationData":[OSD([sQuery(id+"F2.wireOp",EDGE,"E9.MirrorCS"),sQuery(id+"F2.wireOp",EDGE,"E27.MirrorCS")])]});
            var Q85;
            Q85=makeQuery(id+"F3.opExtrude","SWEPT_EDGE",EDGE,{"disambiguationData":[OSD([sQuery(id+"F2.wireOp",EDGE,"E9.MirrorCS"),sQuery(id+"F2.wireOp",EDGE,"E11.MirrorCS")])]});
            var Q86;
            Q86=makeQuery(id+"F3.opExtrude","SWEPT_EDGE",EDGE,{"disambiguationData":[OSD([sQuery(id+"F2.wireOp",EDGE,"E11.MirrorCS"),sQuery(id+"F2.wireOp",EDGE,"E26.MirrorCS")])]});
            var Q87;
            Q87=makeQuery(id+"F3.opExtrude","SWEPT_EDGE",EDGE,{"disambiguationData":[OSD([sQuery(id+"F2.wireOp",EDGE,"E14.MirrorCS"),sQuery(id+"F2.wireOp",EDGE,"E26.MirrorCS")])]});
            var Q88;
            Q88=makeQuery(id+"F3.opExtrude","SWEPT_EDGE",EDGE,{"disambiguationData":[OSD([sQuery(id+"F2.wireOp",EDGE,"E7.MirrorCS"),sQuery(id+"F2.wireOp",EDGE,"E27.MirrorCS")])]});
            var Q89;
            Q89=makeQuery(id+"F3.opExtrude","SWEPT_EDGE",EDGE,{"disambiguationData":[OSD([sQuery(id+"F2.wireOp",EDGE,"E7.MirrorCS"),sQuery(id+"F2.wireOp",EDGE,"E14.MirrorCS")])]});
            var Q90;
            Q90=makeQuery(id+"F3.opExtrude","SWEPT_EDGE",EDGE,{"disambiguationData":[OSD([sQuery(id+"F2.wireOp",EDGE,"E4.0.1.4"),sQuery(id+"F2.wireOp",EDGE,"E4.0.1.5")])]});
            var Q91;
            Q91=makeQuery(id+"F3.opExtrude","SWEPT_EDGE",EDGE,{"disambiguationData":[OSD([sQuery(id+"F2.wireOp",EDGE,"E4.0.1.5"),sQuery(id+"F2.wireOp",EDGE,"E4.0.1.7")])]});
            var Q92;
            Q92=makeQuery(id+"F3.opExtrude","SWEPT_EDGE",EDGE,{"disambiguationData":[OSD([sQuery(id+"F2.wireOp",EDGE,"E4.0.1.6"),sQuery(id+"F2.wireOp",EDGE,"E4.0.1.7")])]});
            var Q93;
            Q93=makeQuery(id+"F3.opExtrude","SWEPT_EDGE",EDGE,{"disambiguationData":[OSD([sQuery(id+"F2.wireOp",EDGE,"E4.0.1.1"),sQuery(id+"F2.wireOp",EDGE,"E4.0.1.6")])]});
            var Q94;
            Q94=makeQuery(id+"F3.opExtrude","SWEPT_EDGE",EDGE,{"disambiguationData":[OSD([sQuery(id+"F2.wireOp",EDGE,"E4.0.1.0"),sQuery(id+"F2.wireOp",EDGE,"E4.0.1.1")])]});
            var Q95;
            Q95=makeQuery(id+"F3.opExtrude","SWEPT_EDGE",EDGE,{"disambiguationData":[OSD([sQuery(id+"F2.wireOp",EDGE,"E4.0.1.0"),sQuery(id+"F2.wireOp",EDGE,"E4.0.1.4")])]});
            var Q96;
            Q96=makeQuery(id+"F3.opExtrude","SWEPT_EDGE",EDGE,{"disambiguationData":[OSD([sQuery(id+"F2.wireOp",EDGE,"E4.1.1.5"),sQuery(id+"F2.wireOp",EDGE,"E4.1.1.7")])]});
            var Q97;
            Q97=makeQuery(id+"F3.opExtrude","SWEPT_EDGE",EDGE,{"disambiguationData":[OSD([sQuery(id+"F2.wireOp",EDGE,"E4.1.1.6"),sQuery(id+"F2.wireOp",EDGE,"E4.1.1.7")])]});
            var Q98;
            Q98=makeQuery(id+"F3.opExtrude","SWEPT_EDGE",EDGE,{"disambiguationData":[OSD([sQuery(id+"F2.wireOp",EDGE,"E4.1.1.1"),sQuery(id+"F2.wireOp",EDGE,"E4.1.1.6")])]});
            var Q99;
            Q99=makeQuery(id+"F3.opExtrude","SWEPT_EDGE",EDGE,{"disambiguationData":[OSD([sQuery(id+"F2.wireOp",EDGE,"E4.1.1.4"),sQuery(id+"F2.wireOp",EDGE,"E4.1.1.5")])]});
            var Q100;
            Q100=makeQuery(id+"F3.opExtrude","SWEPT_EDGE",EDGE,{"disambiguationData":[OSD([sQuery(id+"F2.wireOp",EDGE,"E4.1.1.0"),sQuery(id+"F2.wireOp",EDGE,"E4.1.1.4")])]});
            var Q101;
            Q101=makeQuery(id+"F3.opExtrude","SWEPT_EDGE",EDGE,{"disambiguationData":[OSD([sQuery(id+"F2.wireOp",EDGE,"E4.1.1.0"),sQuery(id+"F2.wireOp",EDGE,"E4.1.1.1")])]});
            var Q102;
            Q102=makeQuery(id+"F3.opExtrude","SWEPT_EDGE",EDGE,{"disambiguationData":[OSD([sQuery(id+"F2.wireOp",EDGE,"E4.2.1.4"),sQuery(id+"F2.wireOp",EDGE,"E4.2.1.5")])]});
            var Q103;
            Q103=makeQuery(id+"F3.opExtrude","SWEPT_EDGE",EDGE,{"disambiguationData":[OSD([sQuery(id+"F2.wireOp",EDGE,"E4.2.1.0"),sQuery(id+"F2.wireOp",EDGE,"E4.2.1.4")])]});
            var Q104;
            Q104=makeQuery(id+"F3.opExtrude","SWEPT_EDGE",EDGE,{"disambiguationData":[OSD([sQuery(id+"F2.wireOp",EDGE,"E4.2.1.0"),sQuery(id+"F2.wireOp",EDGE,"E4.2.1.1")])]});
            var Q105;
            Q105=makeQuery(id+"F3.opExtrude","SWEPT_EDGE",EDGE,{"disambiguationData":[OSD([sQuery(id+"F2.wireOp",EDGE,"E4.2.1.1"),sQuery(id+"F2.wireOp",EDGE,"E4.2.1.6")])]});
            var Q106;
            Q106=makeQuery(id+"F3.opExtrude","SWEPT_EDGE",EDGE,{"disambiguationData":[OSD([sQuery(id+"F2.wireOp",EDGE,"E4.2.1.5"),sQuery(id+"F2.wireOp",EDGE,"E4.2.1.7")])]});
            var Q107;
            Q107=makeQuery(id+"F3.opExtrude","SWEPT_EDGE",EDGE,{"disambiguationData":[OSD([sQuery(id+"F2.wireOp",EDGE,"E4.2.1.6"),sQuery(id+"F2.wireOp",EDGE,"E4.2.1.7")])]});
            var Q108;
            Q108=makeQuery(id+"F3.opExtrude","SWEPT_EDGE",EDGE,{"disambiguationData":[OSD([sQuery(id+"F2.wireOp",EDGE,"E8.MirrorCS"),sQuery(id+"F2.wireOp",EDGE,"E18.MirrorCS")])]});
            var Q109;
            Q109=makeQuery(id+"F3.opExtrude","SWEPT_EDGE",EDGE,{"disambiguationData":[OSD([sQuery(id+"F2.wireOp",EDGE,"E8.MirrorCS"),sQuery(id+"F2.wireOp",EDGE,"E28.MirrorCS")])]});
            var Q110;
            Q110=makeQuery(id+"F3.opExtrude","SWEPT_EDGE",EDGE,{"disambiguationData":[OSD([sQuery(id+"F2.wireOp",EDGE,"E16.MirrorCS"),sQuery(id+"F2.wireOp",EDGE,"E28.MirrorCS")])]});
            var Q111;
            Q111=makeQuery(id+"F3.opExtrude","SWEPT_EDGE",EDGE,{"disambiguationData":[OSD([sQuery(id+"F2.wireOp",EDGE,"E16.MirrorCS"),sQuery(id+"F2.wireOp",EDGE,"E24.MirrorCS")])]});
            var Q112;
            Q112=makeQuery(id+"F3.opExtrude","SWEPT_EDGE",EDGE,{"disambiguationData":[OSD([sQuery(id+"F2.wireOp",EDGE,"E18.MirrorCS"),sQuery(id+"F2.wireOp",EDGE,"E22.MirrorCS")])]});
            var Q113;
            Q113=makeQuery(id+"F3.opExtrude","SWEPT_EDGE",EDGE,{"disambiguationData":[OSD([sQuery(id+"F2.wireOp",EDGE,"E22.MirrorCS"),sQuery(id+"F2.wireOp",EDGE,"E24.MirrorCS")])]});
            var Q114;
            Q114=makeQuery(id+"F3.opExtrude","SWEPT_EDGE",EDGE,{"disambiguationData":[OSD([sQuery(id+"F2.wireOp",EDGE,"E4.0.2.4"),sQuery(id+"F2.wireOp",EDGE,"E4.0.2.5")])]});
            var Q115;
            Q115=makeQuery(id+"F3.opExtrude","SWEPT_EDGE",EDGE,{"disambiguationData":[OSD([sQuery(id+"F2.wireOp",EDGE,"E4.0.2.0"),sQuery(id+"F2.wireOp",EDGE,"E4.0.2.4")])]});
            var Q116;
            Q116=makeQuery(id+"F3.opExtrude","SWEPT_EDGE",EDGE,{"disambiguationData":[OSD([sQuery(id+"F2.wireOp",EDGE,"E4.0.2.0"),sQuery(id+"F2.wireOp",EDGE,"E4.0.2.1")])]});
            var Q117;
            Q117=makeQuery(id+"F3.opExtrude","SWEPT_EDGE",EDGE,{"disambiguationData":[OSD([sQuery(id+"F2.wireOp",EDGE,"E4.0.2.1"),sQuery(id+"F2.wireOp",EDGE,"E4.0.2.6")])]});
            var Q118;
            Q118=makeQuery(id+"F3.opExtrude","SWEPT_EDGE",EDGE,{"disambiguationData":[OSD([sQuery(id+"F2.wireOp",EDGE,"E4.0.2.5"),sQuery(id+"F2.wireOp",EDGE,"E4.0.2.7")])]});
            var Q119;
            Q119=makeQuery(id+"F3.opExtrude","SWEPT_EDGE",EDGE,{"disambiguationData":[OSD([sQuery(id+"F2.wireOp",EDGE,"E4.0.2.6"),sQuery(id+"F2.wireOp",EDGE,"E4.0.2.7")])]});
            var Q120;
            Q120=makeQuery(id+"F3.opExtrude","SWEPT_EDGE",EDGE,{"disambiguationData":[OSD([sQuery(id+"F2.wireOp",EDGE,"E4.1.2.4"),sQuery(id+"F2.wireOp",EDGE,"E4.1.2.5")])]});
            var Q121;
            Q121=makeQuery(id+"F3.opExtrude","SWEPT_EDGE",EDGE,{"disambiguationData":[OSD([sQuery(id+"F2.wireOp",EDGE,"E4.1.2.5"),sQuery(id+"F2.wireOp",EDGE,"E4.1.2.7")])]});
            var Q122;
            Q122=makeQuery(id+"F3.opExtrude","SWEPT_EDGE",EDGE,{"disambiguationData":[OSD([sQuery(id+"F2.wireOp",EDGE,"E4.1.2.6"),sQuery(id+"F2.wireOp",EDGE,"E4.1.2.7")])]});
            var Q123;
            Q123=makeQuery(id+"F3.opExtrude","SWEPT_EDGE",EDGE,{"disambiguationData":[OSD([sQuery(id+"F2.wireOp",EDGE,"E4.1.2.1"),sQuery(id+"F2.wireOp",EDGE,"E4.1.2.6")])]});
            var Q124;
            Q124=makeQuery(id+"F3.opExtrude","SWEPT_EDGE",EDGE,{"disambiguationData":[OSD([sQuery(id+"F2.wireOp",EDGE,"E4.1.2.0"),sQuery(id+"F2.wireOp",EDGE,"E4.1.2.4")])]});
            var Q125;
            Q125=makeQuery(id+"F3.opExtrude","SWEPT_EDGE",EDGE,{"disambiguationData":[OSD([sQuery(id+"F2.wireOp",EDGE,"E4.1.2.0"),sQuery(id+"F2.wireOp",EDGE,"E4.1.2.1")])]});
            fillet(context, id + "F4", {"entities" : qUnion([Q0, Q1, Q2, Q3, Q4, Q5, Q6, Q7, Q8, Q9, Q10, Q11, Q12, Q13, Q14, Q15, Q16, Q17, Q18, Q19, Q20, Q21, Q22, Q23, Q24, Q25, Q26, Q27, Q28, Q29, Q30, Q31, Q32, Q33, Q34, Q35, Q36, Q37, Q38, Q39, Q40, Q41, Q42, Q43, Q44, Q45, Q46, Q47, Q48, Q49, Q50, Q51, Q52, Q53, Q54, Q55, Q56, Q57, Q58, Q59, Q60, Q61, Q62, Q63, Q64, Q65, Q66, Q67, Q68, Q69, Q70, Q71, Q72, Q73, Q74, Q75, Q76, Q77, Q78, Q79, Q80, Q81, Q82, Q83, Q84, Q85, Q86, Q87, Q88, Q89, Q90, Q91, Q92, Q93, Q94, Q95, Q96, Q97, Q98, Q99, Q100, Q101, Q102, Q103, Q104, Q105, Q106, Q107, Q108, Q109, Q110, Q111, Q112, Q113, Q114, Q115, Q116, Q117, Q118, Q119, Q120, Q121, Q122, Q123, Q124, Q125]), "radius" : 2.5 * mm, "tangentPropagation" : true, "allowEdgeOverflow" : false});
        }
        {
            var Q0;
            Q0=makeQuery(id+"F1.opExtrude","CAP_FACE",FACE,{"disambiguationData":[OSD([sQuery(id+"F0.wireOp",EDGE,"E0")])],"isStart":true});
            var sketch = newSketch(context, id + "F5", { "sketchPlane" : qUnion([Q0])});
            skText(sketch, "E55", { "text": "Z", "fontName": "OpenSans-Regular.ttf"});
            skLineSegment(sketch, "E56", {"start": v(0, 0) * mm, "end": v(0, -60) * mm, "construction": true});
            skPoint(sketch, "E57", {"position": v(0, -60) * mm});
            const initialGuessF5  = {"E55": [-0.0062, -0.0675, 1, 0, 0.015]};
            skSetInitialGuess(sketch, initialGuessF5);
            skSolve(sketch);
        }
        {
            var Q0;
            Q0 = qSketchRegion(id + "F5", true);
            extrude(context, id + "F6", {"entities" : qUnion([Q0]), "operationType" : NewBodyOperationType.REMOVE, "oppositeDirection" : true, "depth" : 0.5 * mm, "offsetDistance" : 25 * mm});
        }
        {
            var Q0;
            Q0=makeQuery(id+"F1.opExtrude","CAP_FACE",FACE,{"disambiguationData":[OSD([sQuery(id+"F0.wireOp",EDGE,"E0")])],"isStart":false});
            var sketch = newSketch(context, id + "F7", { "sketchPlane" : qUnion([Q0])});
            skLineSegment(sketch, "E58", {"start": v(0, 0) * mm, "end": v(-56.57, -56.57) * mm, "construction": true});
            skLineSegment(sketch, "E59", {"start": v(-56.57, -56.57) * mm, "end": v(56.57, -56.57) * mm, "construction": true});
            skLineSegment(sketch, "E60", {"start": v(56.57, -56.57) * mm, "end": v(0, 0) * mm, "construction": true});
            skLineSegment(sketch, "E61", {"start": v(0, 0) * mm, "end": v(0, -56.57) * mm, "construction": true});
            skPoint(sketch, "E62", {"position": v(0, -56.57) * mm});
            skText(sketch, "E63", { "text": "X", "fontName": "OpenSans-Regular.ttf"});
            skPoint(sketch, "E64", {"position": v(-56.57, -56.57) * mm});
            skText(sketch, "E65", { "text": "Y\n", "fontName": "OpenSans-Regular.ttf"});
            skPoint(sketch, "E66", {"position": v(56.57, -56.57) * mm});
            const initialGuessF7  = {"E63": [-0.06189, -0.06257, 1, 0, 0.012], "E65": [0.05136, -0.06257, 1, 0, 0.012]};
            skSetInitialGuess(sketch, initialGuessF7);
            skSolve(sketch);
        }
        {
            var Q0;
            Q0 = qSketchRegion(id + "F7", true);
            extrude(context, id + "F8", {"entities" : qUnion([Q0]), "operationType" : NewBodyOperationType.REMOVE, "oppositeDirection" : true, "depth" : 0.5 * mm, "offsetDistance" : 25 * mm});
        }
        {
            var Q0;
            Q0=makeQuery(id+"F1.opExtrude","CAP_EDGE",EDGE,{"disambiguationData":[OSD([sQuery(id+"F0.wireOp",EDGE,"E0")])],"isStart":true});
            chamfer(context, id + "F9", {"entities" : qUnion([Q0]), "width" : 1 * mm, "tangentPropagation" : true});
        }
    });
